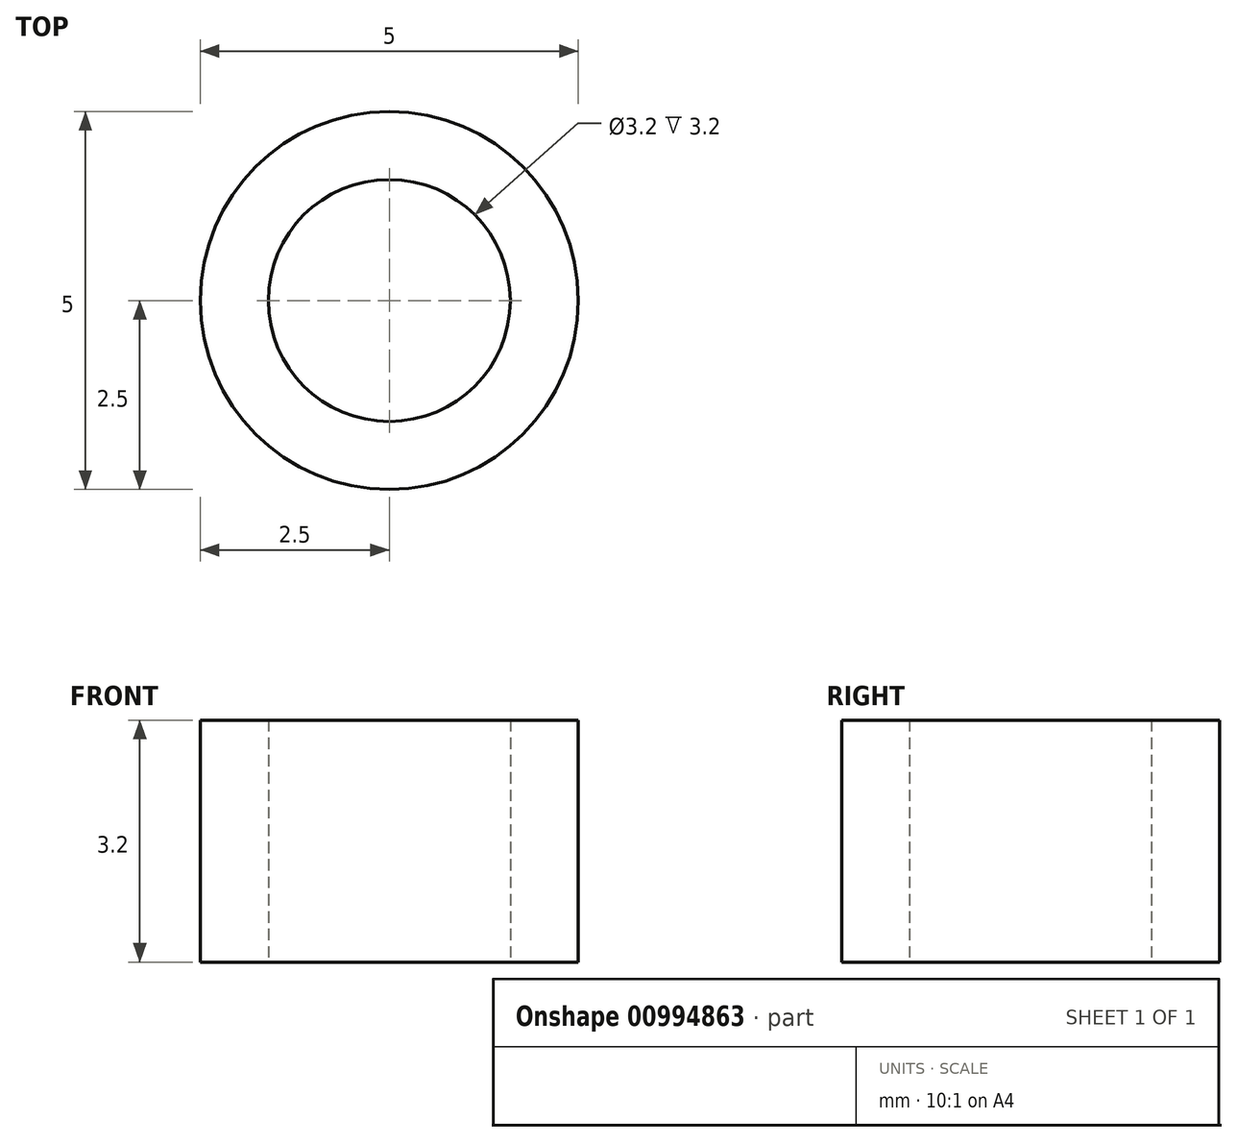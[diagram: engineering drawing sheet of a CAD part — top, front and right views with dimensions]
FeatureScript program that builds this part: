
annotation { "Feature Type Name" : "Feature", "Feature Type Description" : "" }
export const myFeature = defineFeature(function(context is Context, id is Id, definition is map)
    precondition{}
    {
        {
            var Q0;
            Q0=qCreatedBy(makeId("Top.planeOp"),FACE);
            var sketch = newSketch(context, id + "F0", { "sketchPlane" : qUnion([Q0])});
            skCircle(sketch, "E0", {"center": v(0, 0) * mm, "radius": 1.6 * mm});
            skCircle(sketch, "E1", {"center": v(0, 0) * mm, "radius": 2.5 * mm});
            skSolve(sketch);
        }
        {
            var Q0;
            Q0 = qSketchRegion(id + "F0", true);
            extrude(context, id + "F1", {"entities" : qUnion([Q0]), "depth" : 3.2 * mm, "offsetDistance" : 25 * mm});
        }
    });
